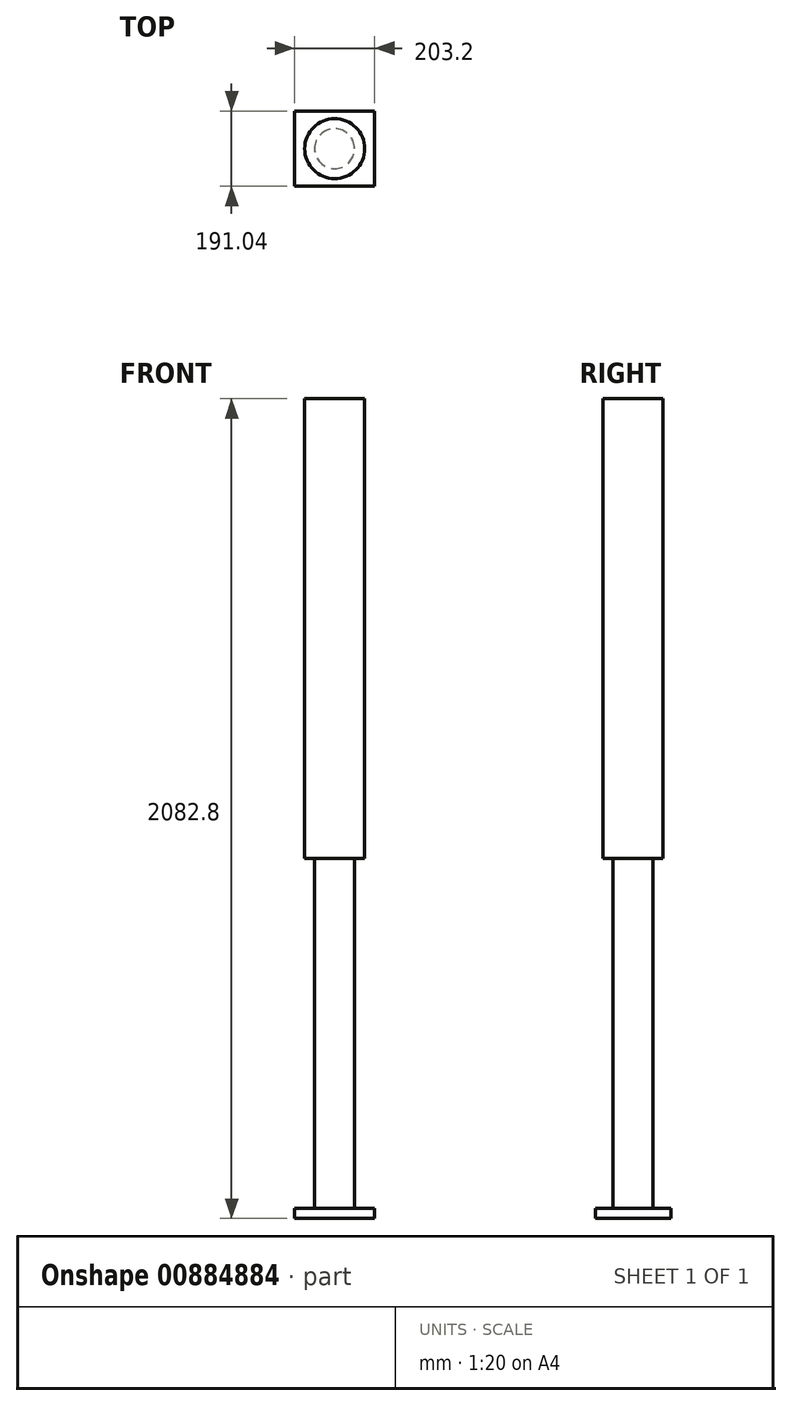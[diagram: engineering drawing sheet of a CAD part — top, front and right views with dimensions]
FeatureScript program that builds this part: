
annotation { "Feature Type Name" : "Feature", "Feature Type Description" : "" }
export const myFeature = defineFeature(function(context is Context, id is Id, definition is map)
    precondition{}
    {
        {
            var Q0;
            Q0=qCreatedBy(makeId("Right.planeOp"),FACE);
            var sketch = newSketch(context, id + "F0", { "sketchPlane" : qUnion([Q0])});
            skLineSegment(sketch, "E0", {"start": v(0, 0) * mm, "end": v(-50.8, 0) * mm});
            skLineSegment(sketch, "E1", {"start": v(-50.8, 0) * mm, "end": v(-50.8, 914.4) * mm});
            skLineSegment(sketch, "E2", {"start": v(-50.8, 914.4) * mm, "end": v(-76.2, 914.4) * mm});
            skLineSegment(sketch, "E3", {"start": v(-76.2, 914.4) * mm, "end": v(-76.2, 2082.8) * mm});
            skLineSegment(sketch, "E4", {"start": v(-76.2, 2082.8) * mm, "end": v(0, 2082.8) * mm});
            skLineSegment(sketch, "E5", {"start": v(0, 2082.8) * mm, "end": v(0, 0) * mm});
            skSolve(sketch);
        }
        {
            var Q0;
            Q0=makeQuery(id+"F0.imprint","IMPRINT",FACE,{"disambiguationData":[TD([[makeQuery(id+"F0.imprint","IMPRINT",EDGE,{"derivedFrom":sQuery(id+"F0.wireOp",EDGE,"E0")}),-1.0]])]});
            var Q1;
            Q1=sQuery(id+"F0.wireOp",EDGE,"E5");
            revolve(context, id + "F1", {"surfaceOperationType" : NewSurfaceOperationType.NEW, "entities" : qUnion([Q0]), "axis" : qUnion([Q1]), "revolveType" : RevolveType.FULL});
        }
        {
            var Q0;
            Q0=qCreatedBy(makeId("Top.planeOp"),FACE);
            var sketch = newSketch(context, id + "F2", { "sketchPlane" : qUnion([Q0])});
            skLineSegment(sketch, "E6.bottom", {"start": v(101.6, 95.52) * mm, "end": v(-101.6, 95.52) * mm});
            skLineSegment(sketch, "E6.top", {"start": v(101.6, -95.52) * mm, "end": v(-101.6, -95.52) * mm});
            skLineSegment(sketch, "E6.left", {"start": v(101.6, 95.52) * mm, "end": v(101.6, -95.52) * mm});
            skLineSegment(sketch, "E6.right", {"start": v(-101.6, 95.52) * mm, "end": v(-101.6, -95.52) * mm});
            skPoint(sketch, "E6.middle", {"position": v(0, 0) * mm});
            skSolve(sketch);
        }
        {
            var Q0;
            Q0=makeQuery(id+"F2.imprint","IMPRINT",FACE,{"disambiguationData":[TD([[makeQuery(id+"F2.imprint","IMPRINT",EDGE,{"derivedFrom":sQuery(id+"F2.wireOp",EDGE,"E6.bottom")}),1.0]])]});
            extrude(context, id + "F3", {"entities" : qUnion([Q0]), "operationType" : NewBodyOperationType.ADD, "depth" : 25.4 * mm, "offsetDistance" : 25.4 * mm});
        }
    });
